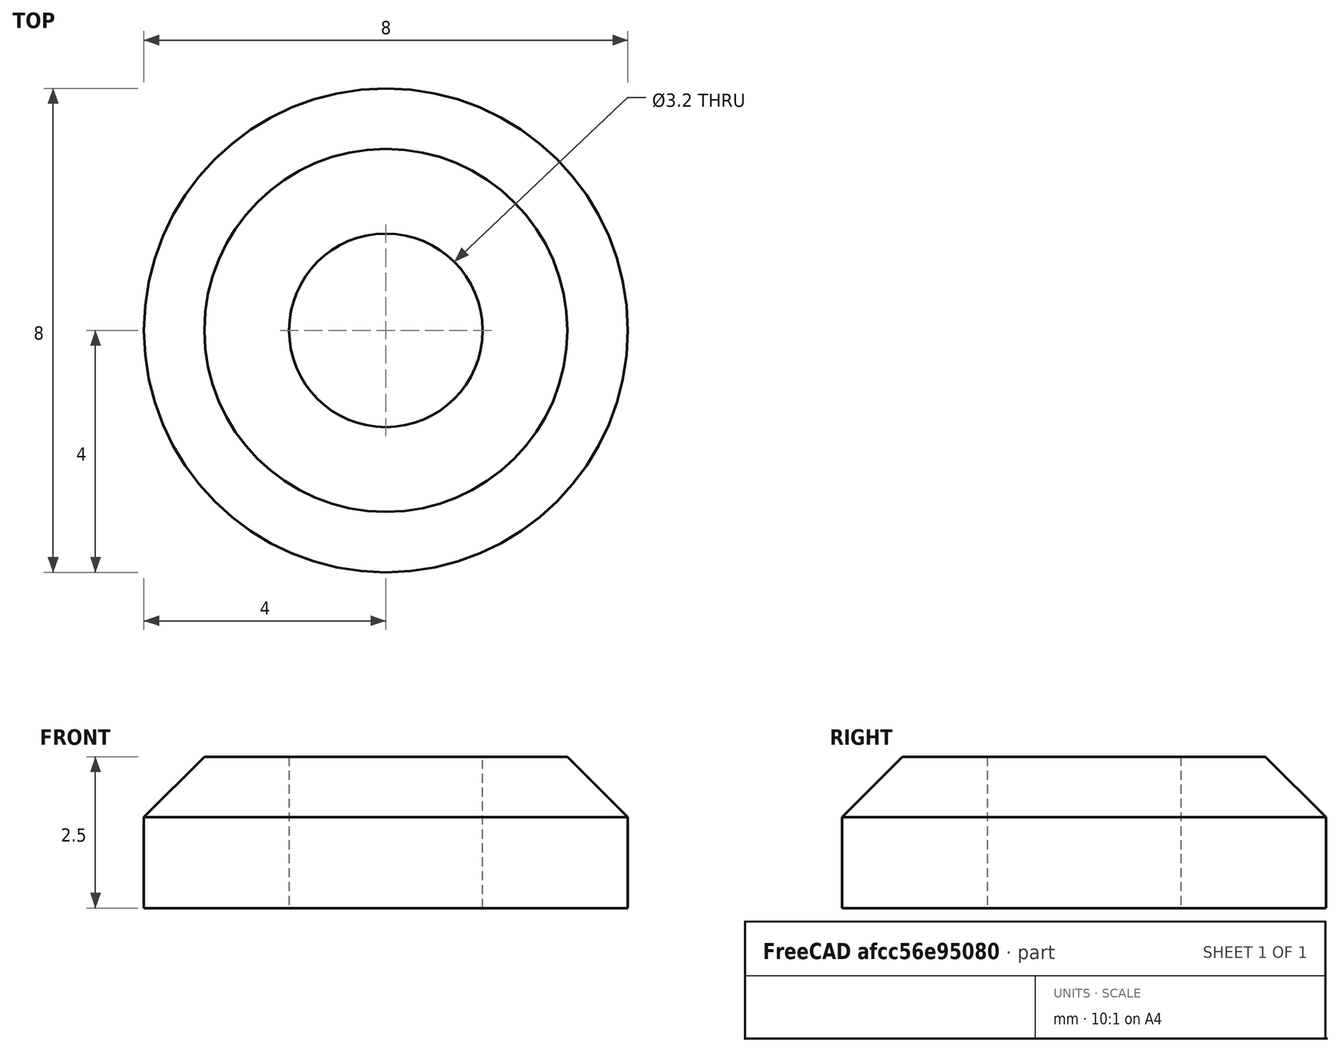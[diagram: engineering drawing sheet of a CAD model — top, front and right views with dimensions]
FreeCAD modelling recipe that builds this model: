
FCSTD DOCUMENT  (FreeCAD 0.20R29603 (Git))
Label: 8000-3200-2500
License: All rights reserved
LicenseURL: http://en.wikipedia.org/wiki/All_rights_reserved
objects: Sketcher::SketchObject×1, PartDesign::Pad×1, PartDesign::Chamfer×1, PartDesign::Body×1
note: 6 computed .brp shape members not serialized (recipe doc carries the construction recipe); baked Part::Feature solids carry a one-line shape summary decoded from their .brp

FEATURE [Sketcher::SketchObject] Sketch
  FullyConstrained = true
  MapMode = 5
  Support = -> [XY_Plane]
  sketch-geometry (4):
    g0: Circle CenterX=0 CenterY=0 CenterZ=0 NormalX=0 NormalY=0 NormalZ=1 AngleXU=0 Radius=4
    g1: Circle CenterX=0 CenterY=0 CenterZ=0 NormalX=0 NormalY=0 NormalZ=1 AngleXU=0 Radius=1.6
    g2: GeomPoint X=4 Y=0 Z=0
    g3: GeomPoint X=1.6 Y=0 Z=0
  constraints (8):
    c: Coincident(g0,g-1)
    c: Coincident(g1,g0)
    c: Radius(g1) = 1.6
    c: PointOnObject(g3,g1)
    c: PointOnObject(g3,g-1)
    c: PointOnObject(g2,g0)
    c: PointOnObject(g2,g-1)
    c: Radius(g0) = 4
FEATURE [PartDesign::Pad] Pad
  Direction = (0,0,1)
  Length = 2.5
  Length2 = 10
  Profile = -> Sketch
  ReferenceAxis = -> Sketch [N_Axis]
  Type = 0
FEATURE [PartDesign::Chamfer] Chamfer
  Angle = 45
  Base = -> Pad [Edge3]
  BaseFeature = -> Pad
  ChamferType = 0
  FlipDirection = false
  Size = 1
  Size2 = 1
  SupportTransform = false
  UseAllEdges = false
FEATURE [PartDesign::Body] Body
  Group = -> [Sketch,Pad,Chamfer]
  Origin = -> Origin
  Tip = -> Chamfer
